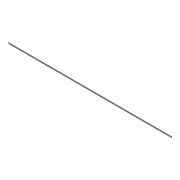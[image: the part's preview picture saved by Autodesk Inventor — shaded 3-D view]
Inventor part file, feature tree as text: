
AUTODESK INVENTOR PART (.ipt)
format: ipt  version: 2012 (Build 160160000, 160)  size: 62,976 bytes
history: native  units: in
note: dims shown in document units (in); Inventor stores cm internally (conversion verified against a paired STEP export)
features: extrude x1, sketch x1
ambient origin geometry x8: Origin, YZ Plane, XZ Plane, XY Plane, X Axis, Y Axis, Z Axis, Center Point
bodies: Solid1 (feature_tree)
feature tree (2):
  extrude  "Extrusion1"  Depth=324.0in
  sketch  "Sketch1"  dims[d0=2.0in d1=324.0in d2=0.188in d3=0.0in]
